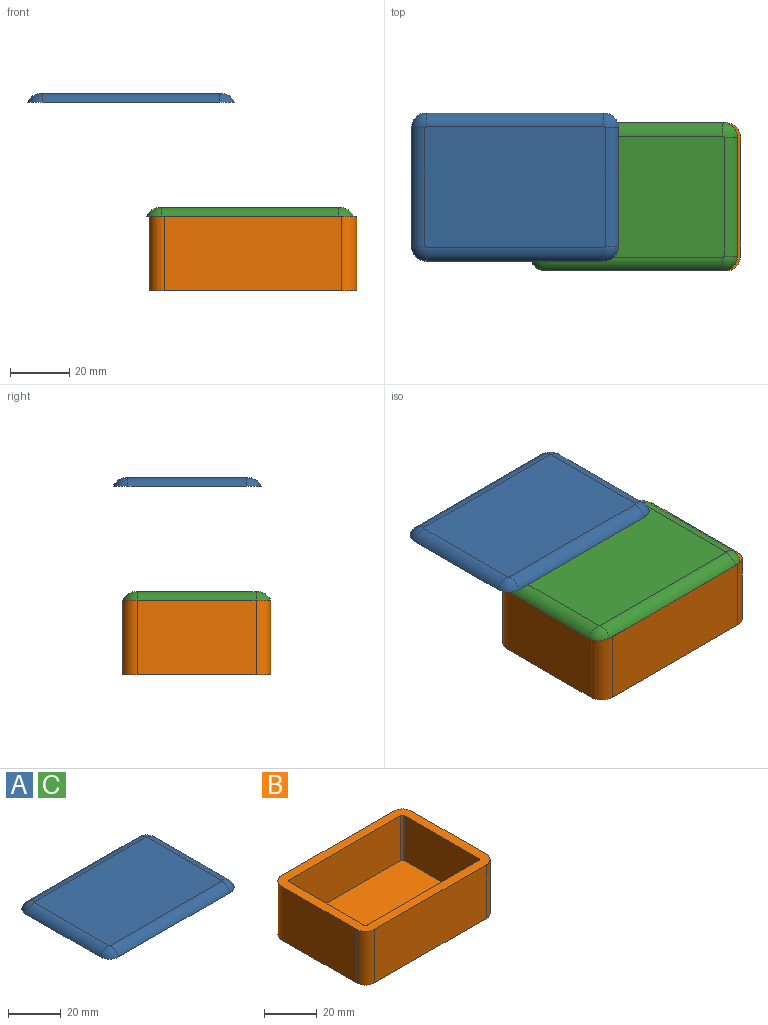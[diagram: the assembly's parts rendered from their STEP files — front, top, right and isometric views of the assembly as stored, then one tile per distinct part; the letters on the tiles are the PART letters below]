
ASSEMBLY  parts=3 mates=1
PART A: 10 faces, bbox 70x50x3 mm
  f0: plane 60.84x40.84mm, normal (0,0,1), area 2484mm2, adj f2,f3,f4,f5,f6,f7,f8,f9
  f1: plane 70x50mm, normal (0,0,-1), area 3478.5mm2, adj f2,f3,f4,f5,f6,f7,f8,f9
  f2: cylinder r=5mm len=40mm, axis (0,-1,0), area 231.9mm2, adj f0,f1,f3,f4
  f3: torus R=0.42mm, axis (0,0,-1), area 27.4mm2, adj f0,f1,f2,f5
  f4: torus R=0.42mm, axis (0,0,-1), area 27.4mm2, adj f0,f1,f2,f6
  f5: cylinder r=5mm len=60mm, axis (1,0,0), area 347.8mm2, adj f0,f1,f3,f7
  f6: cylinder r=5mm len=60mm, axis (1,0,0), area 347.8mm2, adj f0,f1,f4,f8
  f7: torus R=0.42mm, axis (0,0,-1), area 27.4mm2, adj f0,f1,f5,f9
  f8: torus R=0.42mm, axis (0,0,-1), area 27.4mm2, adj f0,f1,f6,f9
  f9: cylinder r=5mm len=40mm, axis (0,-1,0), area 231.9mm2, adj f0,f1,f7,f8
PART B: 19 faces, bbox 70x50x25 mm
  f0: plane 70x50mm, normal (0,0,1), area 875.4mm2, adj f1,f2,f3,f4,f5,f6,f7,f8
  f1: plane 40x25mm, normal (1,0,0), area 1000mm2, adj f0,f2,f8,f9
  f2: cylinder r=5mm len=25mm, axis (0,0,-1), area 196.3mm2, adj f0,f1,f3,f9
  f3: plane 60x25mm, normal (0,1,0), area 1500mm2, adj f0,f2,f4,f9
  f4: cylinder r=5mm len=25mm, axis (0,0,-1), area 196.3mm2, adj f0,f3,f5,f9
  f5: plane 40x25mm, normal (-1,0,0), area 1000mm2, adj f0,f4,f6,f9
  f6: cylinder r=5mm len=25mm, axis (0,0,-1), area 196.3mm2, adj f0,f5,f7,f9
  f7: plane 60x25mm, normal (0,-1,0), area 1500mm2, adj f0,f6,f8,f9
  f8: cylinder r=5mm len=25mm, axis (0,0,-1), area 196.3mm2, adj f0,f1,f7,f9
  f9: plane 70x50mm, normal (0,0,-1), area 3478.5mm2, adj f1,f2,f3,f4,f5,f6,f7,f8
  f10: plane 40x21mm, normal (-1,0,0), area 840mm2, adj f0,f11,f17,f18
  f11: cylinder r=1mm len=21mm, axis (0,0,-1), area 33mm2, adj f0,f10,f12,f18
  f12: plane 60x21mm, normal (0,-1,0), area 1260mm2, adj f0,f11,f13,f18
  f13: cylinder r=1mm len=21mm, axis (0,0,-1), area 33mm2, adj f0,f12,f14,f18
  f14: plane 40x21mm, normal (1,0,0), area 840mm2, adj f0,f13,f15,f18
  f15: cylinder r=1mm len=21mm, axis (0,0,-1), area 33mm2, adj f0,f14,f16,f18
  f16: plane 60x21mm, normal (0,1,0), area 1260mm2, adj f0,f15,f17,f18
  f17: cylinder r=1mm len=21mm, axis (0,0,-1), area 33mm2, adj f0,f10,f16,f18
  f18: plane 62x42mm, normal (0,0,1), area 2603.1mm2, adj f10,f11,f12,f13,f14,f15,f16,f17
PART C: same geometry as A
PLACE A t=(7.27,41.07,49.24)mm
PLACE B t=(48.45,37.85,-14.28)mm
PLACE C t=(47.45,37.85,10.72)mm
MATE slider B.f0 <-> C.f3  axis (0,0,1) through (17.45,57.85,10.72)mm
